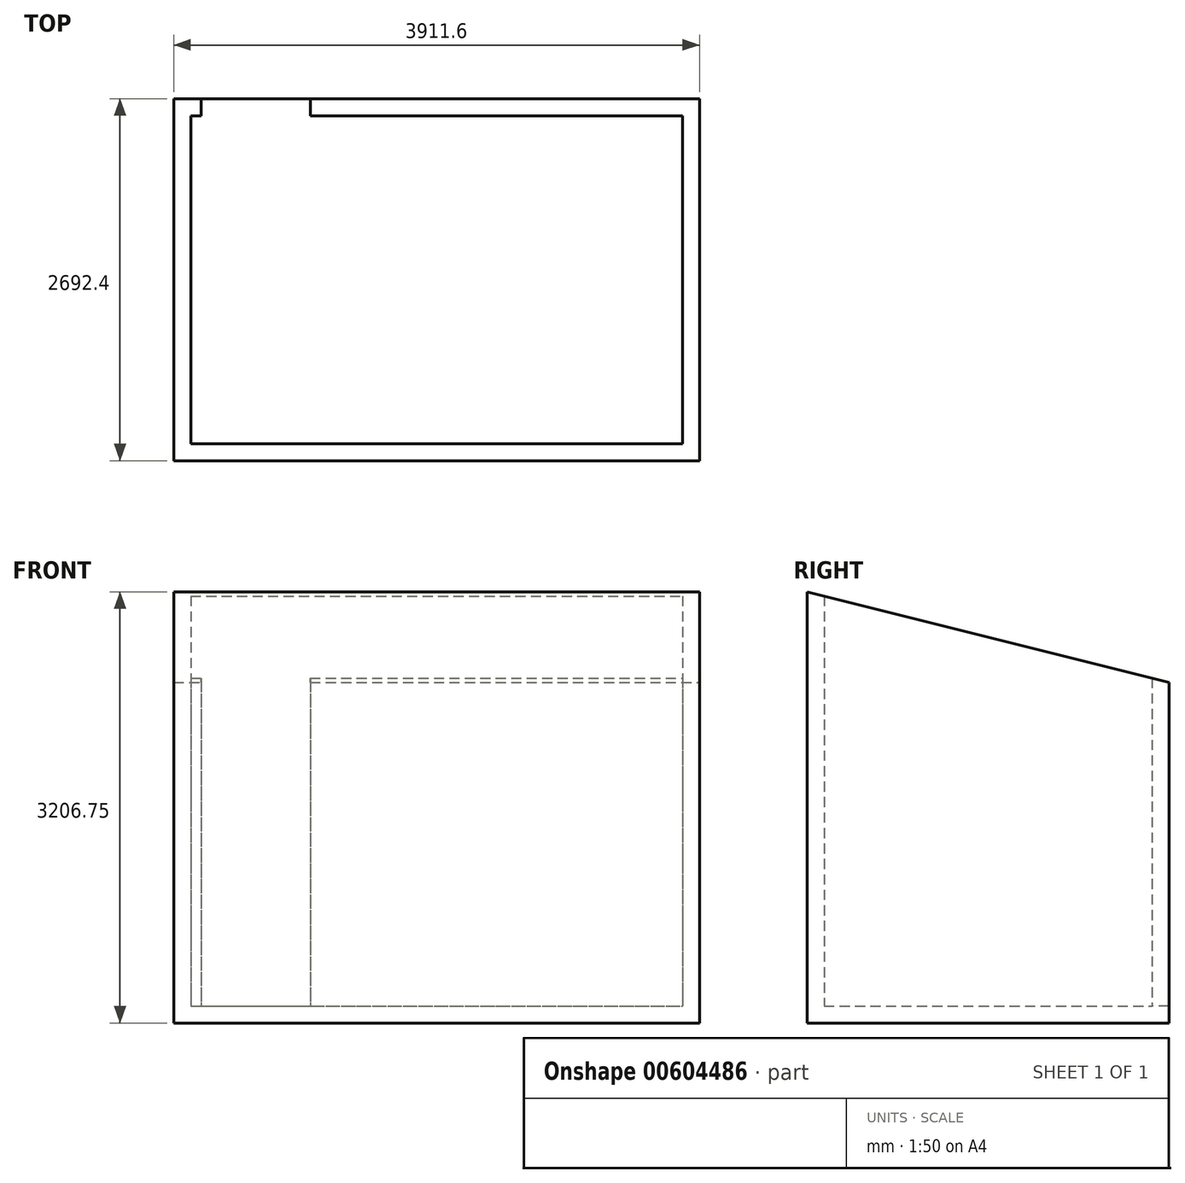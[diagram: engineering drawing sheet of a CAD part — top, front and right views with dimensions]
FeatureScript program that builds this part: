
annotation { "Feature Type Name" : "Feature", "Feature Type Description" : "" }
export const myFeature = defineFeature(function(context is Context, id is Id, definition is map)
    precondition{}
    {
        {
            var Q0;
            Q0=qCreatedBy(makeId("Top.planeOp"),FACE);
            var sketch = newSketch(context, id + "F0", { "sketchPlane" : qUnion([Q0])});
            skLineSegment(sketch, "E0.bottom", {"start": v(0, 0) * mm, "end": v(3657.6, 0) * mm});
            skLineSegment(sketch, "E0.top", {"start": v(0, 2438.4) * mm, "end": v(76.2, 2438.4) * mm});
            skLineSegment(sketch, "E0.left", {"start": v(0, 0) * mm, "end": v(0, 2438.4) * mm});
            skLineSegment(sketch, "E0.right", {"start": v(3657.6, 0) * mm, "end": v(3657.6, 2438.4) * mm});
            skLineSegment(sketch, "E1.0", {"start": v(-127, -127) * mm, "end": v(-127, 2565.4) * mm});
            skLineSegment(sketch, "E1.1", {"start": v(-127, -127) * mm, "end": v(3784.6, -127) * mm});
            skLineSegment(sketch, "E1.2", {"start": v(3784.6, -127) * mm, "end": v(3784.6, 2565.4) * mm});
            skLineSegment(sketch, "E1.3", {"start": v(-127, 2565.4) * mm, "end": v(76.2, 2565.4) * mm});
            skLineSegment(sketch, "E2", {"start": v(76.2, 2565.4) * mm, "end": v(76.2, 2438.4) * mm});
            skLineSegment(sketch, "E3", {"start": v(889, 2565.4) * mm, "end": v(889, 2438.4) * mm});
            skLineSegment(sketch, "E4.trimOffspring", {"start": v(889, 2438.4) * mm, "end": v(3657.6, 2438.4) * mm});
            skLineSegment(sketch, "E5.trimOffspring", {"start": v(889, 2565.4) * mm, "end": v(3784.6, 2565.4) * mm});
            skSolve(sketch);
        }
        {
            var Q0;
            Q0=qCreatedBy(makeId("Right.planeOp"),FACE);
            var sketch = newSketch(context, id + "F1", { "sketchPlane" : qUnion([Q0])});
            skLineSegment(sketch, "E6", {"start": v(0, 3048) * mm, "end": v(2438.4, 2438.4) * mm});
            skLineSegment(sketch, "E7", {"start": v(0, 0) * mm, "end": v(2438.4, 0) * mm, "construction": true});
            skLineSegment(sketch, "E8", {"start": v(2438.4, 0) * mm, "end": v(2438.4, 2438.4) * mm, "construction": true});
            skLineSegment(sketch, "E9", {"start": v(0, 0) * mm, "end": v(0, 3048) * mm, "construction": true});
            skSolve(sketch);
        }
        {
            var Q0;
            Q0=sQuery(id+"F1.wireOp",EDGE,"E6");
            cPlane(context, id + "F2", {"entities" : qUnion([Q0]), "cplaneType" : CPlaneType.LINE_ANGLE, "offset" : 25.4 * mm, "angle" : 0 * degree, "width" : 152.4 * mm, "height" : 152.4 * mm});
        }
        {
            var Q0;
            Q0 = qSketchRegion(id + "F0", true);
            var Q1;
            Q1=qCreatedBy(id+"F2.planeOp",FACE);
            extrude(context, id + "F3", {"entities" : qUnion([Q0]), "endBound" : BoundingType.UP_TO_SURFACE, "depth" : 25.4 * mm, "endBoundEntityFace" : qUnion([Q1]), "offsetDistance" : 25.4 * mm});
        }
        {
            var Q0;
            Q0=makeQuery(id+"F3.opExtrude","CAP_FACE",FACE,{"disambiguationData":[OSD([sQuery(id+"F0.wireOp",EDGE,"E0.bottom"),sQuery(id+"F0.wireOp",EDGE,"E0.top"),sQuery(id+"F0.wireOp",EDGE,"E0.left"),sQuery(id+"F0.wireOp",EDGE,"E0.right"),sQuery(id+"F0.wireOp",EDGE,"E1.0"),sQuery(id+"F0.wireOp",EDGE,"E1.1"),sQuery(id+"F0.wireOp",EDGE,"E1.2"),sQuery(id+"F0.wireOp",EDGE,"E1.3"),sQuery(id+"F0.wireOp",EDGE,"E2"),sQuery(id+"F0.wireOp",EDGE,"E3"),sQuery(id+"F0.wireOp",EDGE,"E4.trimOffspring"),sQuery(id+"F0.wireOp",EDGE,"E5.trimOffspring")])],"isStart":true});
            var sketch = newSketch(context, id + "F4", { "sketchPlane" : qUnion([Q0])});
            skLineSegment(sketch, "E10.bottom", {"start": v(3784.6, 127) * mm, "end": v(-127, 127) * mm});
            skLineSegment(sketch, "E10.top", {"start": v(3784.6, -2565.4) * mm, "end": v(-127, -2565.4) * mm});
            skLineSegment(sketch, "E10.left", {"start": v(3784.6, 127) * mm, "end": v(3784.6, -2565.4) * mm});
            skLineSegment(sketch, "E10.right", {"start": v(-127, 127) * mm, "end": v(-127, -2565.4) * mm});
            skSolve(sketch);
        }
        {
            var Q0;
            Q0 = qSketchRegion(id + "F4", true);
            extrude(context, id + "F5", {"entities" : qUnion([Q0]), "operationType" : NewBodyOperationType.ADD, "depth" : 127 * mm, "offsetDistance" : 25.4 * mm});
        }
    });
